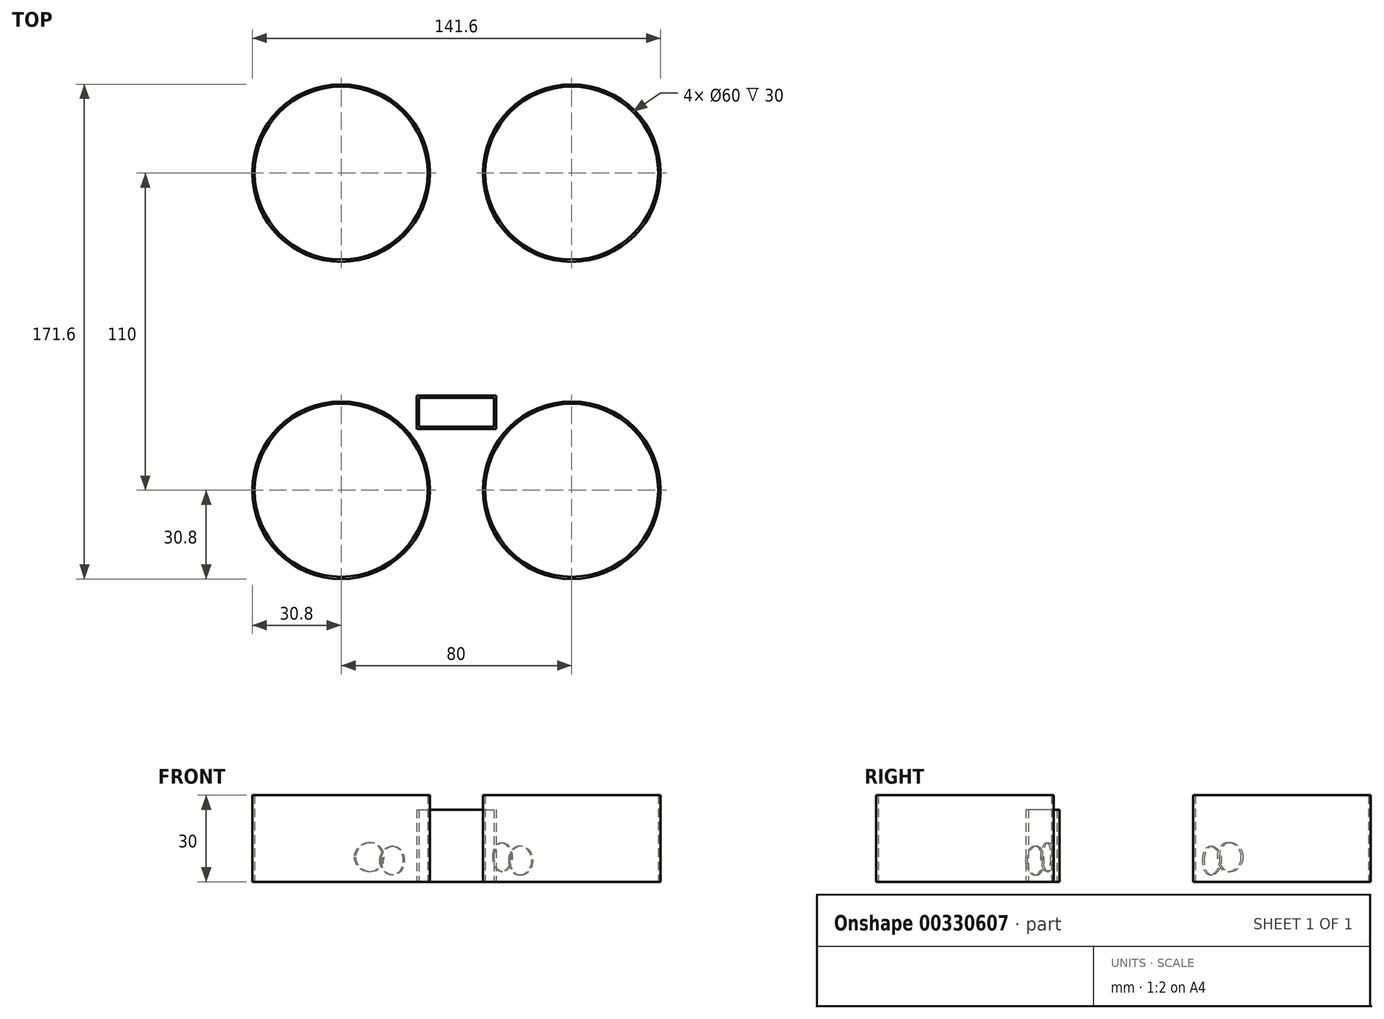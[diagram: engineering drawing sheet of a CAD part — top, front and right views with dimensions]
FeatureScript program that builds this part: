
annotation { "Feature Type Name" : "Feature", "Feature Type Description" : "" }
export const myFeature = defineFeature(function(context is Context, id is Id, definition is map)
    precondition{}
    {
        {
            var Q0;
            Q0=qCreatedBy(makeId("Top.planeOp"),FACE);
            var sketch = newSketch(context, id + "F0", { "sketchPlane" : qUnion([Q0])});
            skCircle(sketch, "E0", {"center": v(-40, 55) * mm, "radius": 30 * mm});
            skCircle(sketch, "E1", {"center": v(-40, 55) * mm, "radius": 30.8 * mm});
            skCircle(sketch, "E2.MirrorC", {"center": v(40, 55) * mm, "radius": 30.8 * mm});
            skCircle(sketch, "E3.MirrorC", {"center": v(40, 55) * mm, "radius": 30 * mm});
            skCircle(sketch, "E4.MirrorC", {"center": v(-40, -55) * mm, "radius": 30.8 * mm});
            skCircle(sketch, "E5.MirrorC", {"center": v(-40, -55) * mm, "radius": 30 * mm});
            skCircle(sketch, "E6.MirrorC", {"center": v(40, -55) * mm, "radius": 30.8 * mm});
            skCircle(sketch, "E7.MirrorC", {"center": v(40, -55) * mm, "radius": 30 * mm});
            skSolve(sketch);
        }
        {
            var Q0;
            Q0=qSketchRegion(id+"F0",true);
            extrude(context, id + "F1", {"entities" : qUnion([Q0]), "depth" : 30 * mm});
        }
        {
            var Q0;
            Q0=qCreatedBy(makeId("Front.planeOp"),FACE);
            var sketch = newSketch(context, id + "F2", { "sketchPlane" : qUnion([Q0])});
            skLineSegment(sketch, "E8", {"start": v(0, 70.13) * mm, "end": v(0, -36.6) * mm, "construction": true});
            skSolve(sketch);
        }
        {
            var Q0;
            Q0=sQuery(id+"F2.wireOp",EDGE,"E8");
            cPlane(context, id + "F3", {"entities" : qUnion([Q0]), "cplaneType" : CPlaneType.LINE_ANGLE, "offset" : 25 * mm, "angle" : 54 * degree, "width" : 150 * mm, "height" : 150 * mm});
        }
        {
            var Q0;
            Q0=qCreatedBy(id+"F3.planeOp",FACE);
            var sketch = newSketch(context, id + "F4", { "sketchPlane" : qUnion([Q0])});
            skCircle(sketch, "E9", {"center": v(0, 7.35) * mm, "radius": 5 * mm});
            skSolve(sketch);
        }
        {
            var Q0;
            Q0=makeQuery(id+"F4.imprint","IMPRINT",FACE,{"disambiguationData":[TD([[makeQuery(id+"F4.imprint","IMPRINT",EDGE,{"derivedFrom":sQuery(id+"F4.wireOp",EDGE,"E9")}),1.0]])]});
            extrude(context, id + "F5", {"entities" : qUnion([Q0]), "operationType" : NewBodyOperationType.REMOVE, "oppositeDirection" : true, "depth" : 60 * mm, "hasSecondDirection" : true, "secondDirectionOppositeDirection" : false, "secondDirectionDepth" : 60 * mm});
        }
        {
            var Q0;
            Q0=sQuery(id+"F2.wireOp",EDGE,"E8");
            cPlane(context, id + "F6", {"entities" : qUnion([Q0]), "cplaneType" : CPlaneType.LINE_ANGLE, "offset" : 25 * mm, "angle" : 126 * degree, "width" : 150 * mm, "height" : 150 * mm});
        }
        {
            var Q0;
            Q0=qCreatedBy(id+"F6.planeOp",FACE);
            var sketch = newSketch(context, id + "F7", { "sketchPlane" : qUnion([Q0])});
            skCircle(sketch, "E10", {"center": v(8.82, 8.55) * mm, "radius": 5 * mm});
            skSolve(sketch);
        }
        {
            var Q0;
            Q0=makeQuery(id+"F7.imprint","IMPRINT",FACE,{"disambiguationData":[TD([[makeQuery(id+"F7.imprint","IMPRINT",EDGE,{"derivedFrom":sQuery(id+"F7.wireOp",EDGE,"E10")}),1.0]])]});
            extrude(context, id + "F8", {"entities" : qUnion([Q0]), "operationType" : NewBodyOperationType.REMOVE, "oppositeDirection" : true, "depth" : 50 * mm, "hasSecondDirection" : true, "secondDirectionOppositeDirection" : false, "secondDirectionDepth" : 50 * mm});
        }
        {
            var Q0;
            Q0=qCreatedBy(makeId("Top.planeOp"),FACE);
            var sketch = newSketch(context, id + "F9", { "sketchPlane" : qUnion([Q0])});
            skLineSegment(sketch, "E11.bottom", {"start": v(-13, -23) * mm, "end": v(13, -23) * mm});
            skLineSegment(sketch, "E11.top", {"start": v(-13, -33) * mm, "end": v(13, -33) * mm});
            skLineSegment(sketch, "E11.left", {"start": v(-13, -23) * mm, "end": v(-13, -33) * mm});
            skLineSegment(sketch, "E11.right", {"start": v(13, -23) * mm, "end": v(13, -33) * mm});
            skLineSegment(sketch, "E12.0", {"start": v(-13.8, -22.2) * mm, "end": v(13.8, -22.2) * mm});
            skLineSegment(sketch, "E12.1", {"start": v(-13.8, -22.2) * mm, "end": v(-13.8, -33.8) * mm});
            skLineSegment(sketch, "E12.2", {"start": v(-13.8, -33.8) * mm, "end": v(13.8, -33.8) * mm});
            skLineSegment(sketch, "E12.3", {"start": v(13.8, -22.2) * mm, "end": v(13.8, -33.8) * mm});
            skSolve(sketch);
        }
        {
            var Q0;
            Q0=qSketchRegion(id+"F9",true);
            extrude(context, id + "F10", {"entities" : qUnion([Q0]), "operationType" : NewBodyOperationType.ADD, "depth" : 25 * mm});
        }
    });
